# Revit family: Accessory-Option-Skirt_Assembly-Murdock_Mfg-SK5_Series
name_source: partatom
category: Specialty Equipment
units: mm (PartAtom-declared; Revit-internal decimal feet)

## family parameters
Cut with Voids When Loaded = No
Host = Face
OmniClass Number = 23.40.20.21
OmniClass Title = Toilet and Bath Specialties
Part Type = Normal
Room Calculation Point = No
Round Connector Dimension = Use Diameter
Shared = Yes

## types (2) — shared parameters
ADA Compliant = Yes
Assembly Code = E2020200
Bottom Access Panel = Yes
Default Elevation = 0"
Description = Accessory: Skirt Assembly for ADA Bi-Level Water Cooler
Height = 6"
Installation Instruction Link = https://www.murdockmfg.com
Installation Type = Wall Mount
Length = 9 3/8"
Manufacturer = Murdock Mfg.
Product Documentation Link = https://www.murdockmfg.com
Product Page URL = https://www.murdockmfg.com
Type Comments = Use with A171-UG & A172-UG series models
URL = https://www.murdockmfg.com
Width = 17 1/2"

## per-type parameters (varying)
| type | Finish | Material |
| A0004000-SK5 | Metal-Murdock Mfg.-Stainless Steel-Satin | Metal-Murdock Mfg.-Stainless Steel-Satin |
| A000G000-SK5 | Steel-Murdock Mfg.-Galvanized-Gray Power Coated | Steel-Murdock Mfg.-Galvanized-Gray Power Coated |

note: column(s) folded — value = type name in every type: Model

## geometry (parser evidence)
native form markers: Sweep x3
no freeform markers — native parametric forms only
